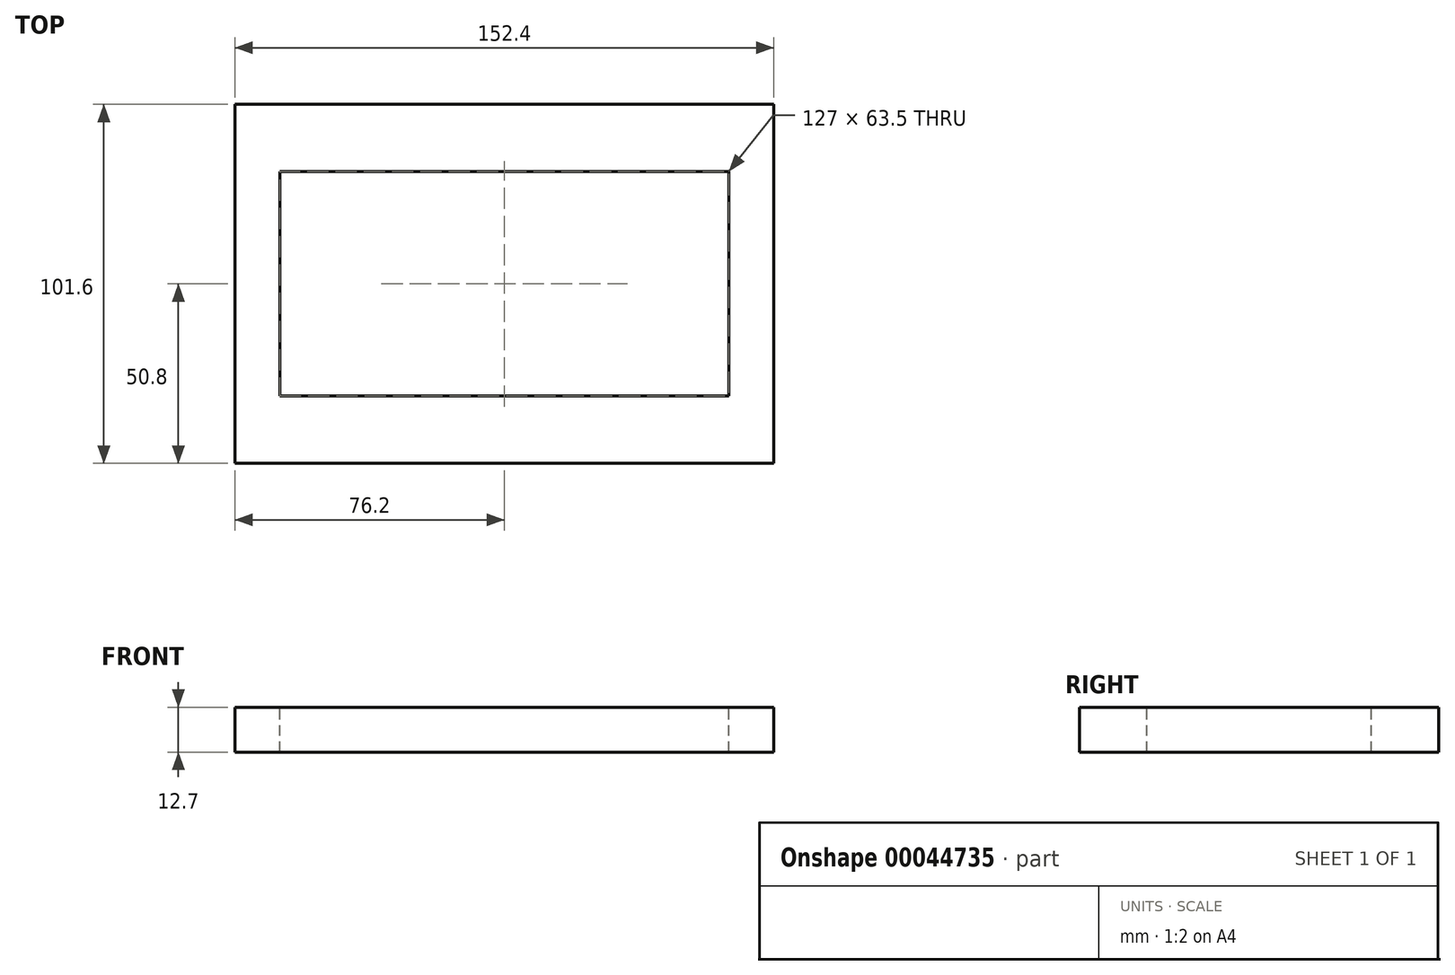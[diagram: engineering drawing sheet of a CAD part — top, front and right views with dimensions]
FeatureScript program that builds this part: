
annotation { "Feature Type Name" : "Feature", "Feature Type Description" : "" }
export const myFeature = defineFeature(function(context is Context, id is Id, definition is map)
    precondition{}
    {
        {
            var Q0;
            Q0=qCreatedBy(makeId("Top.planeOp"),FACE);
            var sketch = newSketch(context, id + "F0", { "sketchPlane" : qUnion([Q0])});
            skLineSegment(sketch, "E0.rect.bottom", {"start": v(76.2, -50.8) * mm, "end": v(-76.2, -50.8) * mm});
            skLineSegment(sketch, "E0.rect.top", {"start": v(76.2, 50.8) * mm, "end": v(-76.2, 50.8) * mm});
            skLineSegment(sketch, "E0.rect.left", {"start": v(76.2, -50.8) * mm, "end": v(76.2, 50.8) * mm});
            skLineSegment(sketch, "E0.rect.right", {"start": v(-76.2, -50.8) * mm, "end": v(-76.2, 50.8) * mm});
            skPoint(sketch, "E0.rect.middle", {"position": v(0, 0) * mm});
            skSolve(sketch);
        }
        {
            var Q0;
            Q0 = qSketchRegion(id + "F0", true);
            extrude(context, id + "F1", {"entities" : qUnion([Q0]), "depth" : 12.7 * mm});
        }
        {
            var Q0;
            Q0=makeQuery(id+"F1.opExtrude","CAP_FACE",FACE,{"disambiguationData":[OSD([sQuery(id+"F0.wireOp",EDGE,"E0.rect.bottom"),sQuery(id+"F0.wireOp",EDGE,"E0.rect.top"),sQuery(id+"F0.wireOp",EDGE,"E0.rect.left"),sQuery(id+"F0.wireOp",EDGE,"E0.rect.right")])],"isStart":false});
            var sketch = newSketch(context, id + "F2", { "sketchPlane" : qUnion([Q0])});
            skLineSegment(sketch, "E1.bottom", {"start": v(-63.5, -31.75) * mm, "end": v(63.5, -31.75) * mm});
            skLineSegment(sketch, "E1.top", {"start": v(-63.5, 31.75) * mm, "end": v(63.5, 31.75) * mm});
            skLineSegment(sketch, "E1.left", {"start": v(-63.5, -31.75) * mm, "end": v(-63.5, 31.75) * mm});
            skLineSegment(sketch, "E1.right", {"start": v(63.5, -31.75) * mm, "end": v(63.5, 31.75) * mm});
            skSolve(sketch);
        }
        {
            var Q0;
            Q0 = qSketchRegion(id + "F2", true);
            extrude(context, id + "F3", {"entities" : qUnion([Q0]), "operationType" : NewBodyOperationType.REMOVE, "oppositeDirection" : true, "depth" : 12.7 * mm});
        }
    });
